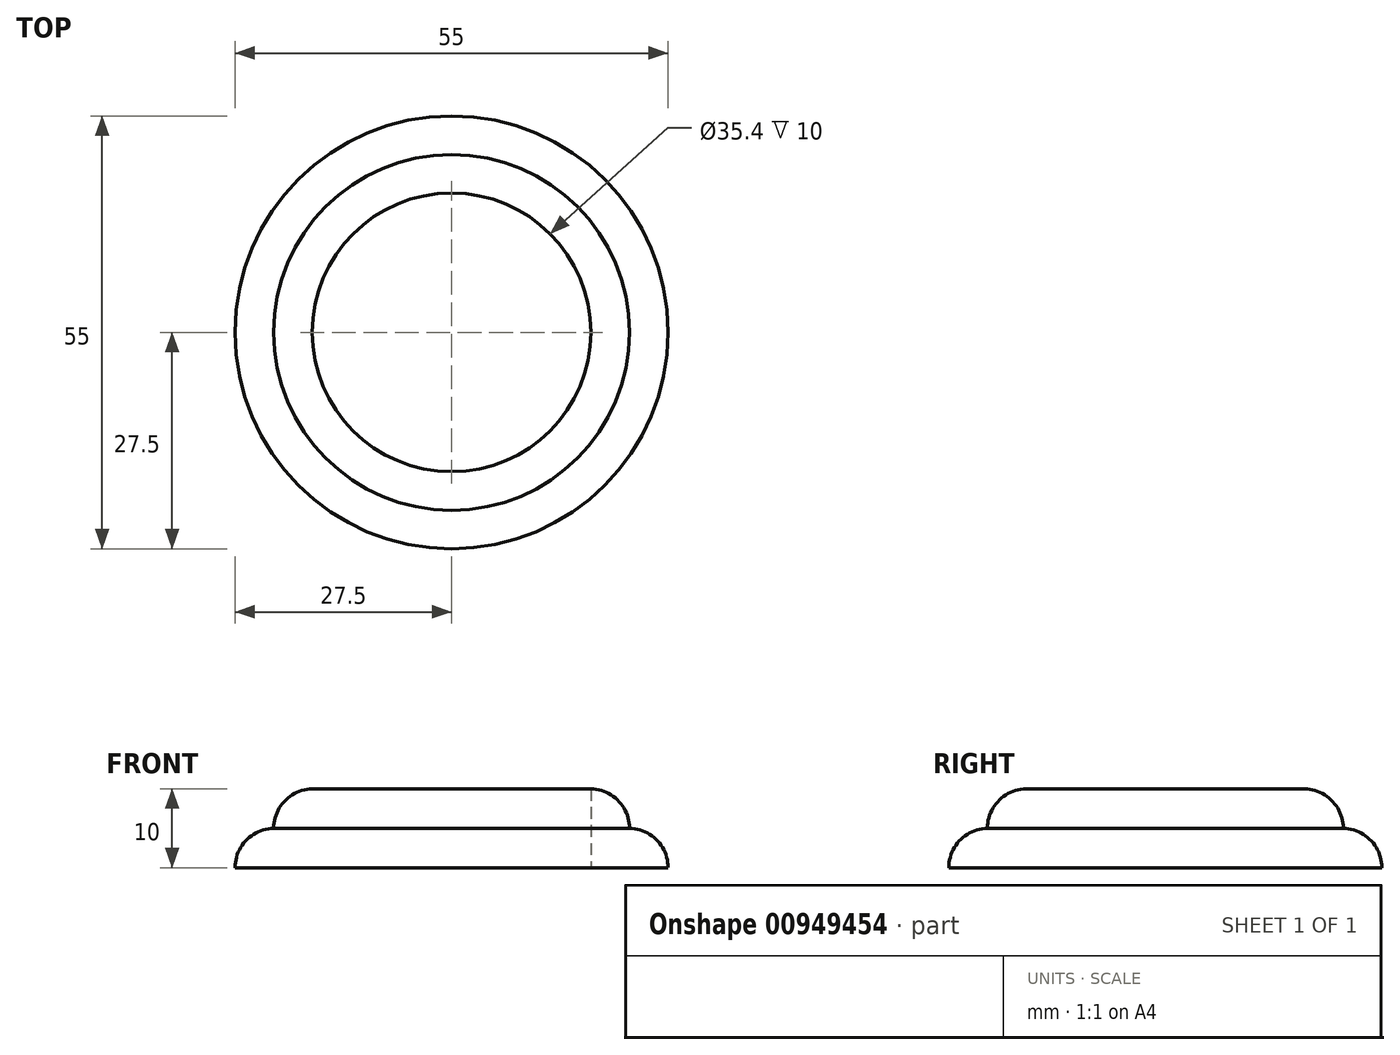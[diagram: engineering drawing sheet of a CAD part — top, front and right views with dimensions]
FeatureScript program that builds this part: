
annotation { "Feature Type Name" : "Feature", "Feature Type Description" : "" }
export const myFeature = defineFeature(function(context is Context, id is Id, definition is map)
    precondition{}
    {
        {
            var Q0;
            Q0=qCreatedBy(makeId("Top.planeOp"),FACE);
            var sketch = newSketch(context, id + "F0", { "sketchPlane" : qUnion([Q0])});
            skCircle(sketch, "E0", {"center": v(0, 0) * mm, "radius": 17.7 * mm});
            skCircle(sketch, "E1", {"center": v(0, 0) * mm, "radius": 27.5 * mm});
            skSolve(sketch);
        }
        {
            var Q0;
            Q0=makeQuery(id+"F0.imprint","IMPRINT",FACE,{"disambiguationData":[TD([[makeQuery(id+"F0.imprint","IMPRINT",EDGE,{"derivedFrom":sQuery(id+"F0.wireOp",EDGE,"E0")}),-1.0]])]});
            extrude(context, id + "F1", {"entities" : qUnion([Q0]), "depth" : 5 * mm, "offsetDistance" : 25 * mm});
        }
        {
            var Q0;
            Q0=makeQuery(id+"F1.opExtrude","CAP_FACE",FACE,{"disambiguationData":[OSD([sQuery(id+"F0.wireOp",EDGE,"E0"),sQuery(id+"F0.wireOp",EDGE,"E1")])],"isStart":false});
            var sketch = newSketch(context, id + "F2", { "sketchPlane" : qUnion([Q0])});
            skCircle(sketch, "E2", {"center": v(0, 0) * mm, "radius": 22.6 * mm});
            skPoint(sketch, "E3.start.orphan", {"position": v(22.6, 0) * mm});
            skPoint(sketch, "E4.orphan", {"position": v(17.7, 0) * mm});
            skPoint(sketch, "E5.end.orphan", {"position": v(27.5, 0) * mm});
            skSolve(sketch);
        }
        {
            var Q0;
            Q0=makeQuery(id+"F2.imprint","IMPRINT",FACE,{"disambiguationData":[TD([[makeQuery(id+"F2.imprint","IMPRINT",EDGE,{"derivedFrom":sQuery(id+"F2.wireOp",EDGE,"E2")}),1.0]])]});
            extrude(context, id + "F3", {"entities" : qUnion([Q0]), "operationType" : NewBodyOperationType.ADD, "depth" : 5 * mm, "offsetDistance" : 25 * mm});
        }
        {
            var Q0;
            Q0=makeQuery(id+"F3.opExtrude","CAP_EDGE",EDGE,{"disambiguationData":[OSD([sQuery(id+"F2.wireOp",EDGE,"E2")])],"isStart":false});
            var Q1;
            Q1=makeQuery(id+"F1.opExtrude","CAP_EDGE",EDGE,{"disambiguationData":[OSD([sQuery(id+"F0.wireOp",EDGE,"E1")])],"isStart":false});
            fillet(context, id + "F4", {"entities" : qUnion([Q0, Q1]), "radius" : 5 * mm, "tangentPropagation" : true, "allowEdgeOverflow" : false});
        }
    });
